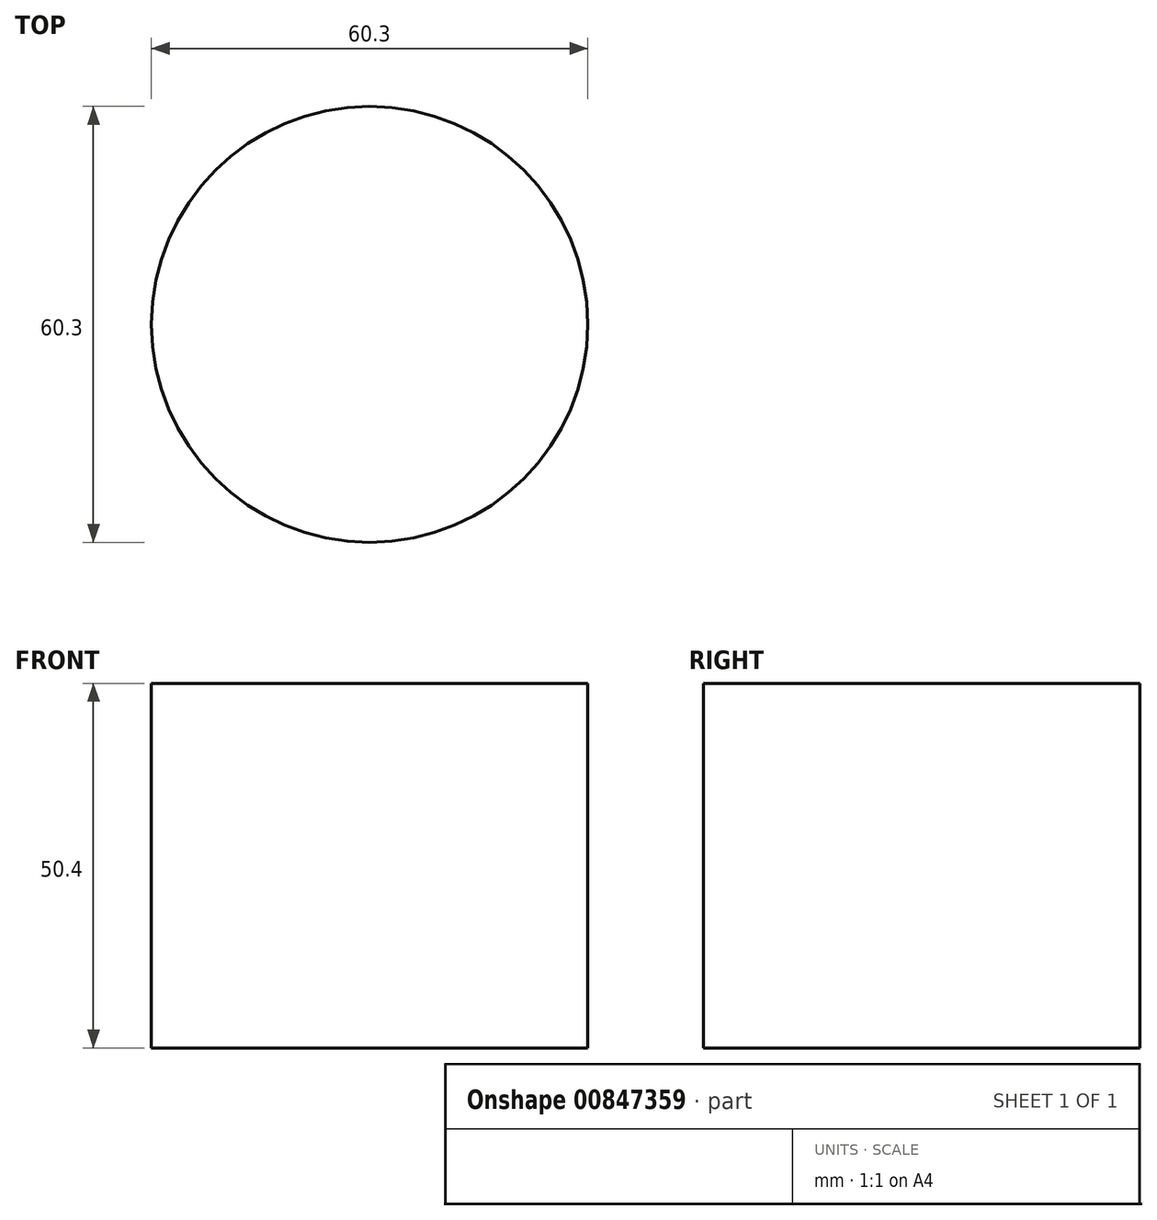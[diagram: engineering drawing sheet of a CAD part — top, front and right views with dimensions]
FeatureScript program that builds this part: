
annotation { "Feature Type Name" : "Feature", "Feature Type Description" : "" }
export const myFeature = defineFeature(function(context is Context, id is Id, definition is map)
    precondition{}
    {
        {
            var Q0;
            Q0=qCreatedBy(makeId("Top.planeOp"),FACE);
            var sketch = newSketch(context, id + "F0", { "sketchPlane" : qUnion([Q0])});
            skCircle(sketch, "E0", {"center": v(0, 0) * mm, "radius": 30.15 * mm});
            skSolve(sketch);
        }
        {
            var Q0;
            Q0 = qSketchRegion(id + "F0", true);
            extrude(context, id + "F1", {"entities" : qUnion([Q0]), "depth" : 50.4 * mm, "offsetDistance" : 25 * mm});
        }
    });
